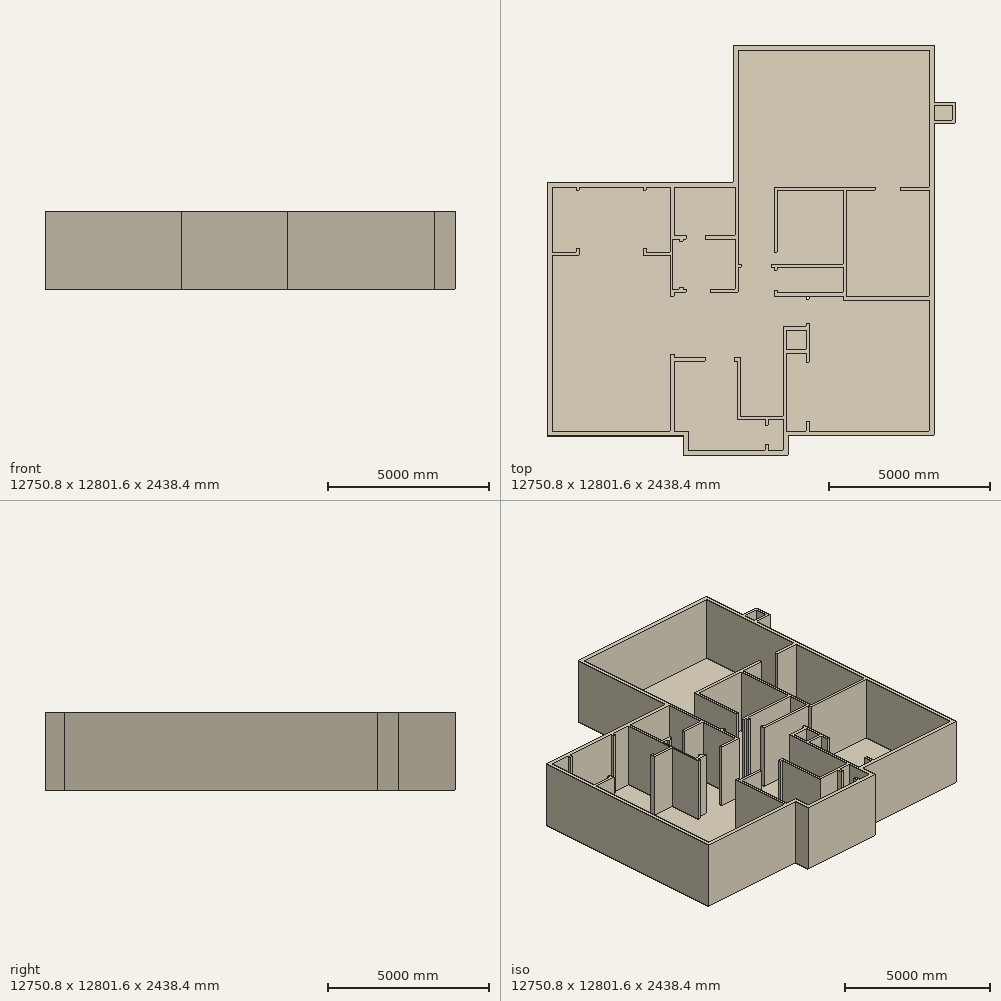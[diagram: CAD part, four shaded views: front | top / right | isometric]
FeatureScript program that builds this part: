
annotation { "Feature Type Name" : "Feature", "Feature Type Description" : "" }
export const myFeature = defineFeature(function(context is Context, id is Id, definition is map)
    precondition{}
    {
        {
            var Q0;
            Q0=qCreatedBy(makeId("Top.planeOp"),FACE);
            var sketch = newSketch(context, id + "F0", { "sketchPlane" : qUnion([Q0])});
            skLineSegment(sketch, "E0", {"start": v(-124.8, 9431.94) * mm, "end": v(6149, 9431.94) * mm});
            skLineSegment(sketch, "E1", {"start": v(-124.8, 9431.94) * mm, "end": v(-124.8, 5164.74) * mm});
            skLineSegment(sketch, "E2", {"start": v(6149, 9431.94) * mm, "end": v(6149, 7653.94) * mm});
            skLineSegment(sketch, "E3", {"start": v(-124.8, 5164.74) * mm, "end": v(-5941.4, 5164.74) * mm});
            skLineSegment(sketch, "E4", {"start": v(-5941.4, 5164.74) * mm, "end": v(-5941.4, -2760.06) * mm});
            skLineSegment(sketch, "E5", {"start": v(-5941.4, -2760.06) * mm, "end": v(-1699.6, -2760.06) * mm});
            skLineSegment(sketch, "E6", {"start": v(-1699.6, -2760.06) * mm, "end": v(-1699.6, -3369.66) * mm});
            skLineSegment(sketch, "E7", {"start": v(-1699.6, -3369.66) * mm, "end": v(1577, -3369.66) * mm});
            skLineSegment(sketch, "E8", {"start": v(1577, -3369.66) * mm, "end": v(1577, -2760.06) * mm});
            skLineSegment(sketch, "E9", {"start": v(1577, -2760.06) * mm, "end": v(6149, -2760.06) * mm});
            skLineSegment(sketch, "E10", {"start": v(27.6, 9279.54) * mm, "end": v(5996.6, 9279.54) * mm});
            skLineSegment(sketch, "E11", {"start": v(5996.6, 9279.54) * mm, "end": v(5996.6, 5012.34) * mm});
            skLineSegment(sketch, "E12", {"start": v(5996.6, -2607.66) * mm, "end": v(2237.4, -2607.66) * mm});
            skLineSegment(sketch, "E13", {"start": v(1424.6, -2607.66) * mm, "end": v(1424.6, -3217.26) * mm});
            skLineSegment(sketch, "E14", {"start": v(1424.6, -3217.26) * mm, "end": v(967.4, -3217.26) * mm});
            skLineSegment(sketch, "E15", {"start": v(-1547.2, -3217.26) * mm, "end": v(-1547.2, -2607.66) * mm});
            skLineSegment(sketch, "E16", {"start": v(-1547.2, -2607.66) * mm, "end": v(-1979, -2607.66) * mm});
            skLineSegment(sketch, "E17", {"start": v(-5789, -2607.66) * mm, "end": v(-5789, 2878.74) * mm});
            skLineSegment(sketch, "E18", {"start": v(-5789, 5012.34) * mm, "end": v(-5027, 5012.34) * mm});
            skLineSegment(sketch, "E19", {"start": v(27.6, 5012.34) * mm, "end": v(27.6, 9279.54) * mm});
            skLineSegment(sketch, "E20", {"start": v(5996.6, 5012.34) * mm, "end": v(5082.2, 5012.34) * mm});
            skLineSegment(sketch, "E21", {"start": v(5082.2, 4910.74) * mm, "end": v(5996.6, 4910.74) * mm});
            skLineSegment(sketch, "E22", {"start": v(5082.2, 5012.34) * mm, "end": v(5082.2, 4910.74) * mm});
            skLineSegment(sketch, "E23", {"start": v(4320.2, 5012.34) * mm, "end": v(1145.2, 5012.34) * mm});
            skLineSegment(sketch, "E24", {"start": v(1145.2, 5012.34) * mm, "end": v(1145.2, 2959.52) * mm});
            skLineSegment(sketch, "E25", {"start": v(1145.2, 2959.52) * mm, "end": v(1246.8, 2959.52) * mm});
            skLineSegment(sketch, "E26", {"start": v(1246.8, 2959.52) * mm, "end": v(1246.8, 4910.74) * mm});
            skLineSegment(sketch, "E27", {"start": v(1246.8, 4910.74) * mm, "end": v(3304.2, 4910.74) * mm});
            skLineSegment(sketch, "E28", {"start": v(4320.2, 4910.74) * mm, "end": v(4320.2, 5012.34) * mm});
            skLineSegment(sketch, "E29", {"start": v(1145.2, 2600.14) * mm, "end": v(1145.2, 2599.34) * mm});
            skLineSegment(sketch, "E30", {"start": v(1145.2, 2599.34) * mm, "end": v(1043.6, 2599.34) * mm});
            skLineSegment(sketch, "E31", {"start": v(1043.6, 2599.34) * mm, "end": v(1043.6, 2497.74) * mm});
            skLineSegment(sketch, "E32", {"start": v(1043.6, 2497.74) * mm, "end": v(1145.2, 2497.74) * mm});
            skLineSegment(sketch, "E33", {"start": v(1145.2, 2497.74) * mm, "end": v(1145.2, 2396.14) * mm});
            skLineSegment(sketch, "E34", {"start": v(1145.2, 2600.14) * mm, "end": v(1246.8, 2600.14) * mm});
            skLineSegment(sketch, "E35", {"start": v(1246.8, 2600.14) * mm, "end": v(1246.8, 2599.34) * mm});
            skLineSegment(sketch, "E36", {"start": v(1246.8, 2599.34) * mm, "end": v(3304.2, 2599.34) * mm});
            skLineSegment(sketch, "E37", {"start": v(3304.2, 2599.34) * mm, "end": v(3304.2, 4910.74) * mm});
            skLineSegment(sketch, "E38", {"start": v(3405.8, 4910.74) * mm, "end": v(3405.8, 2497.74) * mm});
            skLineSegment(sketch, "E39", {"start": v(1145.2, 2396.14) * mm, "end": v(1246.8, 2396.14) * mm});
            skLineSegment(sketch, "E40", {"start": v(1246.8, 2396.14) * mm, "end": v(1246.8, 2497.74) * mm});
            skLineSegment(sketch, "E41", {"start": v(1246.8, 2497.74) * mm, "end": v(3304.2, 2497.74) * mm});
            skLineSegment(sketch, "E42", {"start": v(3405.8, 2497.74) * mm, "end": v(3405.8, 1583.34) * mm});
            skLineSegment(sketch, "E43", {"start": v(3405.8, 1583.34) * mm, "end": v(5996.6, 1583.34) * mm});
            skLineSegment(sketch, "E44", {"start": v(3304.2, 2497.74) * mm, "end": v(3304.2, 1710.34) * mm});
            skLineSegment(sketch, "E45", {"start": v(3304.2, 1481.74) * mm, "end": v(5996.6, 1481.74) * mm});
            skLineSegment(sketch, "E46", {"start": v(3304.2, 1710.34) * mm, "end": v(1246.8, 1710.34) * mm});
            skLineSegment(sketch, "E47", {"start": v(1246.8, 1710.34) * mm, "end": v(1246.8, 1786.54) * mm});
            skLineSegment(sketch, "E48", {"start": v(1246.8, 1786.54) * mm, "end": v(1145.2, 1786.54) * mm});
            skLineSegment(sketch, "E49", {"start": v(1145.2, 1786.54) * mm, "end": v(1145.2, 1608.74) * mm});
            skLineSegment(sketch, "E50", {"start": v(1145.2, 1608.74) * mm, "end": v(3304.2, 1608.74) * mm});
            skLineSegment(sketch, "E51", {"start": v(1424.6, -2607.66) * mm, "end": v(1424.6, -2252.06) * mm});
            skLineSegment(sketch, "E52", {"start": v(1424.6, 643.54) * mm, "end": v(2135.8, 643.54) * mm});
            skLineSegment(sketch, "E53", {"start": v(2135.8, 643.54) * mm, "end": v(2135.8, 745.14) * mm});
            skLineSegment(sketch, "E54", {"start": v(2135.8, 745.14) * mm, "end": v(2237.4, 745.14) * mm});
            skLineSegment(sketch, "E55", {"start": v(2237.4, 745.14) * mm, "end": v(2237.4, -474.06) * mm});
            skLineSegment(sketch, "E56", {"start": v(2237.4, -474.06) * mm, "end": v(2135.8, -474.06) * mm});
            skLineSegment(sketch, "E57", {"start": v(2135.8, -474.06) * mm, "end": v(2135.8, -169.26) * mm});
            skLineSegment(sketch, "E58", {"start": v(2135.8, -169.26) * mm, "end": v(1526.2, -169.26) * mm});
            skLineSegment(sketch, "E59", {"start": v(1526.2, -67.66) * mm, "end": v(1526.2, 541.94) * mm});
            skLineSegment(sketch, "E60", {"start": v(1526.2, 541.94) * mm, "end": v(2135.8, 541.94) * mm});
            skLineSegment(sketch, "E61", {"start": v(2135.8, 541.94) * mm, "end": v(2135.8, -67.66) * mm});
            skLineSegment(sketch, "E62", {"start": v(2135.8, -67.66) * mm, "end": v(1526.2, -67.66) * mm});
            skLineSegment(sketch, "E63", {"start": v(1526.2, -169.26) * mm, "end": v(1526.2, -2607.66) * mm});
            skLineSegment(sketch, "E64", {"start": v(2237.4, -2302.86) * mm, "end": v(2237.4, -2607.66) * mm});
            skLineSegment(sketch, "E65", {"start": v(2237.4, -2302.86) * mm, "end": v(2135.8, -2302.86) * mm});
            skLineSegment(sketch, "E66", {"start": v(2135.8, -2302.86) * mm, "end": v(2135.8, -2607.66) * mm});
            skLineSegment(sketch, "E67", {"start": v(2135.8, 1608.74) * mm, "end": v(2135.8, 1507.14) * mm});
            skLineSegment(sketch, "E68", {"start": v(2135.8, 1507.14) * mm, "end": v(2237.4, 1507.14) * mm});
            skLineSegment(sketch, "E69", {"start": v(2237.4, 1507.14) * mm, "end": v(2237.4, 1608.74) * mm});
            skLineSegment(sketch, "E70", {"start": v(1424.6, -2252.06) * mm, "end": v(967.4, -2252.06) * mm});
            skLineSegment(sketch, "E71", {"start": v(967.4, -2252.06) * mm, "end": v(967.4, -2429.86) * mm});
            skLineSegment(sketch, "E72", {"start": v(865.8, -2429.86) * mm, "end": v(865.8, -2252.06) * mm});
            skLineSegment(sketch, "E73", {"start": v(865.8, -2252.06) * mm, "end": v(2.2, -2252.06) * mm});
            skLineSegment(sketch, "E74", {"start": v(2.2, -2252.06) * mm, "end": v(2.2, -423.26) * mm});
            skLineSegment(sketch, "E75", {"start": v(2.2, -423.26) * mm, "end": v(-99.4, -423.26) * mm});
            skLineSegment(sketch, "E76", {"start": v(-99.4, -423.26) * mm, "end": v(-99.4, -321.66) * mm});
            skLineSegment(sketch, "E77", {"start": v(-99.4, -321.66) * mm, "end": v(103.8, -321.66) * mm});
            skLineSegment(sketch, "E78", {"start": v(103.8, -321.66) * mm, "end": v(103.8, -2150.46) * mm});
            skLineSegment(sketch, "E79", {"start": v(103.8, -2150.46) * mm, "end": v(1424.6, -2150.46) * mm});
            skLineSegment(sketch, "E80", {"start": v(865.8, -3217.26) * mm, "end": v(865.8, -3039.46) * mm});
            skLineSegment(sketch, "E81", {"start": v(865.8, -3039.46) * mm, "end": v(967.4, -3039.46) * mm});
            skLineSegment(sketch, "E82", {"start": v(967.4, -3039.46) * mm, "end": v(967.4, -3217.26) * mm});
            skLineSegment(sketch, "E83", {"start": v(967.4, -2429.86) * mm, "end": v(865.8, -2429.86) * mm});
            skLineSegment(sketch, "E84.trimOffspring", {"start": v(865.8, -3217.26) * mm, "end": v(-1547.2, -3217.26) * mm});
            skLineSegment(sketch, "E85.trimOffspring", {"start": v(2135.8, -2607.66) * mm, "end": v(1526.2, -2607.66) * mm});
            skLineSegment(sketch, "E86.trimOffspring", {"start": v(3304.2, 1608.74) * mm, "end": v(3304.2, 1481.74) * mm});
            skLineSegment(sketch, "E87.trimOffspring", {"start": v(5996.6, 1481.74) * mm, "end": v(5996.6, -2607.66) * mm});
            skLineSegment(sketch, "E88.trimOffspring", {"start": v(5996.6, 4910.74) * mm, "end": v(5996.6, 1583.34) * mm});
            skLineSegment(sketch, "E89.trimOffspring", {"start": v(3405.8, 4910.74) * mm, "end": v(4320.2, 4910.74) * mm});
            skLineSegment(sketch, "E90", {"start": v(6149, 7653.94) * mm, "end": v(6809.4, 7653.94) * mm});
            skLineSegment(sketch, "E91", {"start": v(6809.4, 7653.94) * mm, "end": v(6809.4, 6993.54) * mm});
            skLineSegment(sketch, "E92", {"start": v(6809.4, 6993.54) * mm, "end": v(6149, 6993.54) * mm});
            skLineSegment(sketch, "E93", {"start": v(6149, 7095.14) * mm, "end": v(6707.8, 7095.14) * mm});
            skLineSegment(sketch, "E94", {"start": v(6707.8, 7095.14) * mm, "end": v(6707.8, 7552.34) * mm});
            skLineSegment(sketch, "E95", {"start": v(6707.8, 7552.34) * mm, "end": v(6149, 7552.34) * mm});
            skLineSegment(sketch, "E96", {"start": v(27.6, 5012.34) * mm, "end": v(27.6, 2599.34) * mm});
            skLineSegment(sketch, "E97", {"start": v(-74, 5012.34) * mm, "end": v(-74, 3488.34) * mm});
            skLineSegment(sketch, "E98", {"start": v(-1979, 5012.34) * mm, "end": v(-1979, 3488.34) * mm});
            skLineSegment(sketch, "E99", {"start": v(-1979, 3488.34) * mm, "end": v(-1598, 3488.34) * mm});
            skLineSegment(sketch, "E100", {"start": v(-1598, 3488.34) * mm, "end": v(-1598, 3386.74) * mm});
            skLineSegment(sketch, "E101", {"start": v(-74, 3488.34) * mm, "end": v(-988.4, 3488.34) * mm});
            skLineSegment(sketch, "E102", {"start": v(-988.4, 3488.34) * mm, "end": v(-988.4, 3386.74) * mm});
            skLineSegment(sketch, "E103", {"start": v(-988.4, 3386.74) * mm, "end": v(-74, 3386.74) * mm});
            skLineSegment(sketch, "E104", {"start": v(-74, 3386.74) * mm, "end": v(-74, 1811.94) * mm});
            skLineSegment(sketch, "E105", {"start": v(-2080.6, 5012.34) * mm, "end": v(-2080.6, 2980.34) * mm});
            skLineSegment(sketch, "E106", {"start": v(-1598, 3386.74) * mm, "end": v(-1699.6, 3386.74) * mm});
            skLineSegment(sketch, "E107", {"start": v(-1699.6, 3386.74) * mm, "end": v(-1699.6, 3310.54) * mm});
            skLineSegment(sketch, "E108", {"start": v(-1699.6, 3310.54) * mm, "end": v(-1801.2, 3310.54) * mm});
            skLineSegment(sketch, "E109", {"start": v(-1801.2, 3310.54) * mm, "end": v(-1801.2, 3386.74) * mm});
            skLineSegment(sketch, "E110", {"start": v(-1801.2, 3386.74) * mm, "end": v(-2029.8, 3386.74) * mm});
            skLineSegment(sketch, "E111", {"start": v(-2029.8, 3386.74) * mm, "end": v(-2029.8, 1811.94) * mm});
            skLineSegment(sketch, "E112.trimOffspring", {"start": v(-1979, 5012.34) * mm, "end": v(-74, 5012.34) * mm});
            skLineSegment(sketch, "E113", {"start": v(-2029.8, 1811.94) * mm, "end": v(-1801.2, 1811.94) * mm});
            skLineSegment(sketch, "E114", {"start": v(-1598, 1811.94) * mm, "end": v(-1598, 1710.34) * mm});
            skLineSegment(sketch, "E115", {"start": v(-1598, 1710.34) * mm, "end": v(-1979, 1710.34) * mm});
            skLineSegment(sketch, "E116", {"start": v(-1801.2, 1811.94) * mm, "end": v(-1801.2, 1888.14) * mm});
            skLineSegment(sketch, "E117", {"start": v(-1801.2, 1888.14) * mm, "end": v(-1699.6, 1888.14) * mm});
            skLineSegment(sketch, "E118", {"start": v(-1699.6, 1888.14) * mm, "end": v(-1699.6, 1811.94) * mm});
            skLineSegment(sketch, "E119.trimOffspring", {"start": v(-1699.6, 1811.94) * mm, "end": v(-1598, 1811.94) * mm});
            skLineSegment(sketch, "E120", {"start": v(-2080.6, 1608.74) * mm, "end": v(-1979, 1608.74) * mm});
            skLineSegment(sketch, "E121", {"start": v(-1979, 1710.34) * mm, "end": v(-1979, 1608.74) * mm});
            skLineSegment(sketch, "E122", {"start": v(-836, 1811.94) * mm, "end": v(-74, 1811.94) * mm});
            skLineSegment(sketch, "E123", {"start": v(27.6, 2599.34) * mm, "end": v(129.2, 2599.34) * mm});
            skLineSegment(sketch, "E124", {"start": v(129.2, 2599.34) * mm, "end": v(129.2, 2497.74) * mm});
            skLineSegment(sketch, "E125", {"start": v(129.2, 2497.74) * mm, "end": v(27.6, 2497.74) * mm});
            skLineSegment(sketch, "E126.trimOffspring", {"start": v(27.6, 2497.74) * mm, "end": v(27.6, 1710.34) * mm});
            skLineSegment(sketch, "E127", {"start": v(-836, 1811.94) * mm, "end": v(-836, 1710.34) * mm});
            skLineSegment(sketch, "E128", {"start": v(-836, 1710.34) * mm, "end": v(27.6, 1710.34) * mm});
            skLineSegment(sketch, "E129", {"start": v(-2080.6, -2607.66) * mm, "end": v(-2080.6, -220.06) * mm});
            skLineSegment(sketch, "E130", {"start": v(-2080.6, -220.06) * mm, "end": v(-1979, -220.06) * mm});
            skLineSegment(sketch, "E131", {"start": v(-1979, -220.06) * mm, "end": v(-1979, -321.66) * mm});
            skLineSegment(sketch, "E132", {"start": v(-1979, -321.66) * mm, "end": v(-1013.8, -321.66) * mm});
            skLineSegment(sketch, "E133", {"start": v(-1013.8, -321.66) * mm, "end": v(-1013.8, -423.26) * mm});
            skLineSegment(sketch, "E134", {"start": v(-1013.8, -423.26) * mm, "end": v(-1979, -423.26) * mm});
            skLineSegment(sketch, "E135", {"start": v(-1979, -423.26) * mm, "end": v(-1979, -2607.66) * mm});
            skLineSegment(sketch, "E136", {"start": v(-5027, 5012.34) * mm, "end": v(-5027, 4910.74) * mm});
            skLineSegment(sketch, "E137", {"start": v(-5027, 4910.74) * mm, "end": v(-4925.4, 4910.74) * mm});
            skLineSegment(sketch, "E138", {"start": v(-4925.4, 4910.74) * mm, "end": v(-4925.4, 5012.34) * mm});
            skLineSegment(sketch, "E139", {"start": v(-5789, 2980.34) * mm, "end": v(-5027, 2980.34) * mm});
            skLineSegment(sketch, "E140", {"start": v(-5027, 2980.34) * mm, "end": v(-5027, 3081.94) * mm});
            skLineSegment(sketch, "E141", {"start": v(-5027, 3081.94) * mm, "end": v(-4925.4, 3081.94) * mm});
            skLineSegment(sketch, "E142", {"start": v(-4925.4, 3081.94) * mm, "end": v(-4925.4, 2878.74) * mm});
            skLineSegment(sketch, "E143", {"start": v(-4925.4, 2878.74) * mm, "end": v(-5789, 2878.74) * mm});
            skLineSegment(sketch, "E144", {"start": v(-2944.2, 5012.34) * mm, "end": v(-2944.2, 4910.74) * mm});
            skLineSegment(sketch, "E145", {"start": v(-2944.2, 4910.74) * mm, "end": v(-2842.6, 4910.74) * mm});
            skLineSegment(sketch, "E146", {"start": v(-2842.6, 4910.74) * mm, "end": v(-2842.6, 5012.34) * mm});
            skLineSegment(sketch, "E147.trimOffspring", {"start": v(-4925.4, 5012.34) * mm, "end": v(-2944.2, 5012.34) * mm});
            skLineSegment(sketch, "E148.trimOffspring", {"start": v(-5789, 2980.34) * mm, "end": v(-5789, 5012.34) * mm});
            skLineSegment(sketch, "E149.trimOffspring", {"start": v(-2842.6, 5012.34) * mm, "end": v(-2080.6, 5012.34) * mm});
            skLineSegment(sketch, "E150", {"start": v(-2080.6, 2878.74) * mm, "end": v(-2944.2, 2878.74) * mm});
            skLineSegment(sketch, "E151", {"start": v(-2944.2, 2878.74) * mm, "end": v(-2944.2, 3081.94) * mm});
            skLineSegment(sketch, "E152", {"start": v(-2944.2, 3081.94) * mm, "end": v(-2842.6, 3081.94) * mm});
            skLineSegment(sketch, "E153", {"start": v(-2842.6, 3081.94) * mm, "end": v(-2842.6, 2980.34) * mm});
            skLineSegment(sketch, "E154", {"start": v(-2842.6, 2980.34) * mm, "end": v(-2080.6, 2980.34) * mm});
            skLineSegment(sketch, "E155.trimOffspring", {"start": v(-2080.6, 2878.74) * mm, "end": v(-2080.6, 1608.74) * mm});
            skLineSegment(sketch, "E156.trimOffspring", {"start": v(6149, 7552.34) * mm, "end": v(6149, 7095.14) * mm});
            skLineSegment(sketch, "E157.trimOffspring", {"start": v(6149, 6993.54) * mm, "end": v(6149, -2760.06) * mm});
            skLineSegment(sketch, "E158.trimOffspring", {"start": v(-2080.6, -2607.66) * mm, "end": v(-5789, -2607.66) * mm});
            skLineSegment(sketch, "E159.trimOffspring", {"start": v(1424.6, -2150.46) * mm, "end": v(1424.6, 643.54) * mm});
            skSolve(sketch);
        }
        {
            var Q0;
            Q0=makeQuery(id+"F0.imprint","IMPRINT",FACE,{"disambiguationData":[TD([[makeQuery(id+"F0.imprint","IMPRINT",EDGE,{"derivedFrom":sQuery(id+"F0.wireOp",EDGE,"E10")}),-1.0]])]});
            var Q1;
            Q1=makeQuery(id+"F0.imprint","IMPRINT",FACE,{"disambiguationData":[TD([[makeQuery(id+"F0.imprint","IMPRINT",EDGE,{"derivedFrom":sQuery(id+"F0.wireOp",EDGE,"E59")}),-1.0]])]});
            var Q2;
            Q2=makeQuery(id+"F0.imprint","IMPRINT",FACE,{"disambiguationData":[TD([[makeQuery(id+"F0.imprint","IMPRINT",EDGE,{"derivedFrom":sQuery(id+"F0.wireOp",EDGE,"E93")}),1.0]])]});
            extrude(context, id + "F1", {"entities" : qUnion([Q0, Q1, Q2]), "depth" : 101.6 * mm});
        }
        {
            var Q0;
            Q0=makeQuery(id+"F0.imprint","IMPRINT",FACE,{"disambiguationData":[TD([[makeQuery(id+"F0.imprint","IMPRINT",EDGE,{"derivedFrom":sQuery(id+"F0.wireOp",EDGE,"E0")}),-1.0]])]});
            extrude(context, id + "F2", {"entities" : qUnion([Q0]), "operationType" : NewBodyOperationType.ADD, "depth" : 2438.4 * mm});
        }
    });
